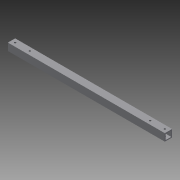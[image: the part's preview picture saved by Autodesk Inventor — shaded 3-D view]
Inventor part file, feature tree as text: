
AUTODESK INVENTOR PART (.ipt)
format: ipt  version: 2015 SP1 (Build 190203100, 203)  size: 105,984 bytes
history: native  units: in
note: dims shown in document units (in); Inventor stores cm internally (conversion verified against a paired STEP export)
features: sketch x2, extrude x1, hole x1, projected_geometry x1
ambient origin geometry x8: Origin, YZ Plane, XZ Plane, XY Plane, X Axis, Y Axis, Z Axis, Center Point
bodies: Solid1 (feature_tree)
feature tree (5):
  extrude  "Extrusion1"  Depth=1.0in
  hole  "Hole3"  [1 undecoded]
  sketch  "Sketch1"  dims[d0=1.0in d1=1.0in]
  sketch  "Sketch2"  dims[d2=0.75in d3=0.75in d4=0.125in d5=0.125in d6=27.5in d7=0.0in d8=0.5in d9=3.5in d10=0.5in d11=0.5in d12=0.5in d13=3.5in d14=0.5in d15=0.5in d23=5.5in d24=0.5in d25=5.0in d26=0.5in d34=0.5in d35=2.0in d36=0.25in d37=0.75in d38=0.375in d39=0.25in d40=0.5635in d41=1.0in d42=0.8108in]
  projected_geometry  "Projected Loop1"
note: 1 required parameter value undecoded (feature->parameter linkage not recoverable at this tier; creation-order binding heuristic only, values carry confidence <= 0.55)
